# Revit family: NBS_PineappleContracts_DmstcChrs_RynoDiningChair
name_source: partatom
category: Furniture
revit_build: Autodesk Revit 2017 (Build: 20171027_0315(x64)
units: mm (PartAtom-declared; Revit-internal decimal feet)

## family parameters
Always vertical = Yes
Cut with Voids When Loaded = No
Room Calculation Point = No
Shared = No
Work Plane-Based = No

## types (1)
- NBS_PineappleContracts_DomesticChairs_RynoDiningChair
    Accessories = Connecting plate
    AssetType = Movable
    BIMObjectName = NBS_PineappleContracts_DomesticChairs_RynoDiningChair
    Category = Pr_40_50_12_22:Dining chairs
    ChairMaterial = NBS_Concept
    ColourOptions = Black, Dark blue, Granite, Light blue, Lime, Orange, Red, White
    Description = Polyethylene dining chair
    DurationUnit = year
    ExposedEdges = Rounded
    FabricLocationOptions = None (RYND), Upholstered back (RYNDB), Upholstered seat (RYNDS), Upholstered back and seat (RYNDSB)
    FabricOptions = A wide choice of fabrics are available
    Features = Difficult to pick up due to flowing, contoured design, rounded top to prevent sitting on the back of the chair, ergonomically designed to give excellent comfort
    Feet = Stainless steel glides
    Finish = Anti-microbial, wipe-clean surface with excellent chemical resistance
    HighestSeatingHeight = 0 mm  [stored 0 ft]
    IfcExportAs = IfcFurnishingElementType
    IfcExportType = CHAIR
    IsBuiltIn = No
    LowestSeatingHeight = 0 mm  [stored 0 ft]
    Manufacturer = www.pineapplecontracts.com
    ManufacturerName = Pineapple Contracts
    ManufacturerURL = www.pineapplecontracts.com
    Material = Polyethylene
    ModelNumber = ARD-000
    ModelReference = Ryno Dining Chair
    NBSCertification = www.nationalbimlibrary.com/cert/wlstw3el
    NBSDescription = Domestic chairs
    NBSReference = 45-35-20/365
    Name = DomesticChairs_RynoDiningChair_PineappleContracts
    NominalDepth = 760 mm
    NominalHeight = 780 mm
    NominalLength = 0 mm  [stored 0 ft]
    NominalWidth = 500 mm
    ProductInformation = www.pineapplecontracts.com/userfiles/file/RYNO-brochure.pdf
    SeatingHeight = 450 mm
    Size = 880 x 500 x 620
    StrengthAndStability = Level 2
    Uniclass2015Code = Pr_40_50_12_22
    Uniclass2015Title = Dining chairs
    Uniclass2015Version = Products v1.5
    Version = 6
    WallThickness = 0 mm  [stored 0 ft]
    WarrantyDescription = Guarantee against manufacturing faults
    WarrantyDurationParts = 7
    WarrantyDurationUnit = year
    Weight = 50 kg

note: [stored X ft] marks values corroborated as IEEE doubles in the binary element streams (Revit-internal decimal feet)

## geometry (parser evidence)
native form markers: Sweep x2
no freeform markers — native parametric forms only
